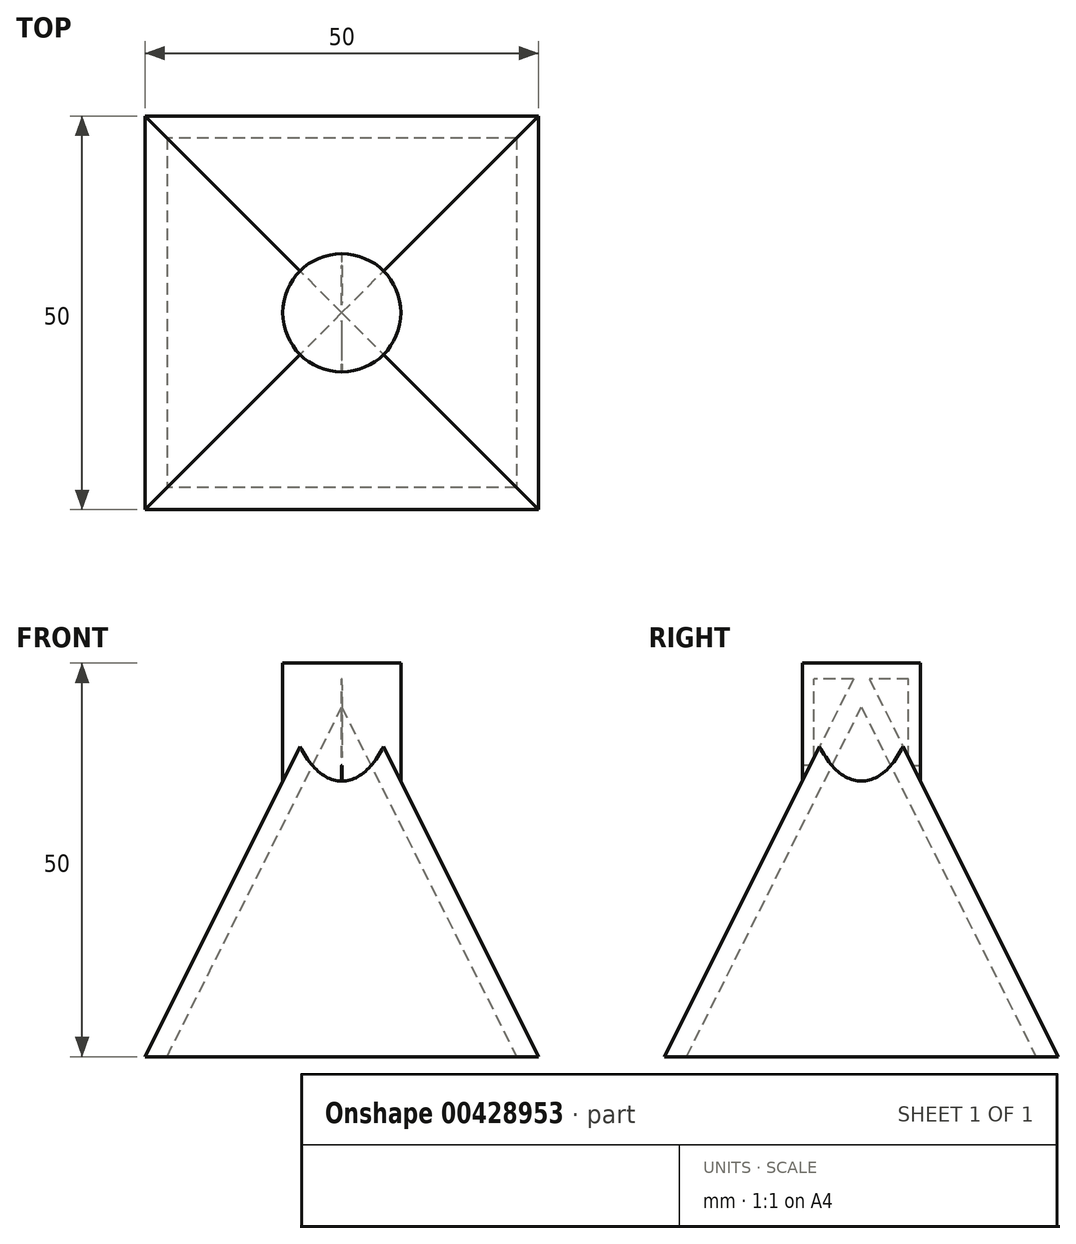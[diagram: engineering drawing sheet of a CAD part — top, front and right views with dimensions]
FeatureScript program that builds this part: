
annotation { "Feature Type Name" : "Feature", "Feature Type Description" : "" }
export const myFeature = defineFeature(function(context is Context, id is Id, definition is map)
    precondition{}
    {
        {
            var Q0;
            Q0=qCreatedBy(makeId("Top.planeOp"),FACE);
            var sketch = newSketch(context, id + "F0", { "sketchPlane" : qUnion([Q0])});
            skLineSegment(sketch, "E0.bottom", {"start": v(25, 25) * mm, "end": v(-25, 25) * mm});
            skLineSegment(sketch, "E0.top", {"start": v(25, -25) * mm, "end": v(-25, -25) * mm});
            skLineSegment(sketch, "E0.left", {"start": v(25, 25) * mm, "end": v(25, -25) * mm});
            skLineSegment(sketch, "E0.right", {"start": v(-25, 25) * mm, "end": v(-25, -25) * mm});
            skPoint(sketch, "E0.middle", {"position": v(0, 0) * mm});
            skSolve(sketch);
        }
        {
            var Q0;
            Q0=makeQuery(id+"F0.imprint","IMPRINT",FACE,{"disambiguationData":[TD([[makeQuery(id+"F0.imprint","IMPRINT",EDGE,{"derivedFrom":sQuery(id+"F0.wireOp",EDGE,"E0.bottom")}),1.0]])]});
            extrude(context, id + "F1", {"entities" : qUnion([Q0]), "depth" : 50 * mm});
        }
        {
            var Q0;
            Q0=makeQuery(id+"F1.opExtrude","SWEPT_FACE",FACE,{"disambiguationData":[OSD([sQuery(id+"F0.wireOp",EDGE,"E0.top")])]});
            var sketch = newSketch(context, id + "F2", { "sketchPlane" : qUnion([Q0])});
            skLineSegment(sketch, "E1", {"start": v(-25, 0) * mm, "end": v(0, 50) * mm});
            skLineSegment(sketch, "E2", {"start": v(0, 50) * mm, "end": v(-25, 50) * mm});
            skLineSegment(sketch, "E3", {"start": v(-25, 50) * mm, "end": v(-25, 0) * mm});
            skLineSegment(sketch, "E4", {"start": v(0, 50) * mm, "end": v(25, 0) * mm});
            skLineSegment(sketch, "E5", {"start": v(25, 0) * mm, "end": v(25, 50) * mm});
            skLineSegment(sketch, "E6", {"start": v(25, 50) * mm, "end": v(0, 50) * mm});
            skSolve(sketch);
        }
        {
            var Q0;
            Q0=makeQuery(id+"F1.opExtrude","SWEPT_FACE",FACE,{"disambiguationData":[OSD([sQuery(id+"F0.wireOp",EDGE,"E0.left")])]});
            var sketch = newSketch(context, id + "F3", { "sketchPlane" : qUnion([Q0])});
            skLineSegment(sketch, "E7", {"start": v(-25, 0) * mm, "end": v(0, 50) * mm});
            skLineSegment(sketch, "E8", {"start": v(0, 50) * mm, "end": v(-25, 50) * mm});
            skLineSegment(sketch, "E9", {"start": v(-25, 50) * mm, "end": v(-25, 1.34) * mm});
            skLineSegment(sketch, "E10", {"start": v(0, 50) * mm, "end": v(25, 50) * mm});
            skLineSegment(sketch, "E11", {"start": v(25, 50) * mm, "end": v(25, 0) * mm});
            skLineSegment(sketch, "E12", {"start": v(25, 0) * mm, "end": v(0, 50) * mm});
            skSolve(sketch);
        }
        {
            var Q0;
            {var subQ0=sQuery(id+"F3.wireOp",EDGE,"E7");Q0=makeQuery(id+"F3.imprint","IMPRINT",FACE,{"disambiguationData":[TD([[makeQuery(id+"F3.imprint","IMPRINT",EDGE,{"derivedFrom":subQ0}),1.0]])]});}
            var Q1;
            Q1=makeQuery(id+"F3.imprint","IMPRINT",FACE,{"disambiguationData":[TD([[makeQuery(id+"F3.imprint","IMPRINT",EDGE,{"derivedFrom":sQuery(id+"F3.wireOp",EDGE,"E10")}),1.0]])]});
            var Q2;
            Q2=makeQuery(id+"F1.opExtrude","SWEPT_FACE",FACE,{"disambiguationData":[OSD([sQuery(id+"F0.wireOp",EDGE,"E0.right")])]});
            extrude(context, id + "F4", {"entities" : qUnion([Q0, Q1]), "operationType" : NewBodyOperationType.REMOVE, "endBound" : BoundingType.UP_TO_SURFACE, "oppositeDirection" : true, "endBoundEntityFace" : qUnion([Q2]), "depth" : 25 * mm});
        }
        {
            var Q0;
            Q0=makeQuery(id+"F2.imprint","IMPRINT",FACE,{"disambiguationData":[TD([[makeQuery(id+"F2.imprint","IMPRINT",EDGE,{"derivedFrom":sQuery(id+"F2.wireOp",EDGE,"E1")}),1.0]])]});
            var Q1;
            Q1=makeQuery(id+"F2.imprint","IMPRINT",FACE,{"disambiguationData":[TD([[makeQuery(id+"F2.imprint","IMPRINT",EDGE,{"derivedFrom":sQuery(id+"F2.wireOp",EDGE,"E4")}),1.0]])]});
            var Q2;
            Q2=makeQuery(id+"F4.boolean.opBoolean","COPY",FACE,{"derivedFrom":makeQuery(id+"F4.opExtrude","SWEPT_FACE",FACE,{"disambiguationData":[OSD([sQuery(id+"F3.wireOp",EDGE,"E12")])]})});
            extrude(context, id + "F5", {"entities" : qUnion([Q0, Q1]), "operationType" : NewBodyOperationType.REMOVE, "endBound" : BoundingType.UP_TO_SURFACE, "oppositeDirection" : true, "endBoundEntityFace" : qUnion([Q2]), "depth" : 25 * mm});
        }
        {
            var Q0;
            Q0=makeQuery(id+"F1.opExtrude","CAP_FACE",FACE,{"disambiguationData":[OSD([sQuery(id+"F0.wireOp",EDGE,"E0.bottom"),sQuery(id+"F0.wireOp",EDGE,"E0.top"),sQuery(id+"F0.wireOp",EDGE,"E0.left"),sQuery(id+"F0.wireOp",EDGE,"E0.right")])],"isStart":true});
            shell(context, id + "F6", {"entities" : qUnion([Q0]), "thickness" : 2.5 * mm});
        }
        {
            var Q0;
            Q0=qCreatedBy(makeId("Front.planeOp"),FACE);
            var sketch = newSketch(context, id + "F7", { "sketchPlane" : qUnion([Q0])});
            skLineSegment(sketch, "E13.bottom", {"start": v(-7.5, 35) * mm, "end": v(7.5, 35) * mm});
            skLineSegment(sketch, "E13.top", {"start": v(-7.5, 50) * mm, "end": v(7.5, 50) * mm});
            skLineSegment(sketch, "E13.left", {"start": v(-7.5, 35) * mm, "end": v(-7.5, 50) * mm});
            skLineSegment(sketch, "E13.right", {"start": v(7.5, 35) * mm, "end": v(7.5, 50) * mm});
            skLineSegment(sketch, "E14", {"start": v(-7.5, 35) * mm, "end": v(0, 50) * mm});
            skLineSegment(sketch, "E15", {"start": v(0, 50) * mm, "end": v(7.5, 35) * mm});
            skLineSegment(sketch, "E16", {"start": v(0, 50) * mm, "end": v(0, 35) * mm});
            skSolve(sketch);
        }
        {
            var Q0;
            {var subQ0=sQuery(id+"F7.wireOp",EDGE,"E13.left");Q0=makeQuery(id+"F7.imprint","IMPRINT",FACE,{"disambiguationData":[TD([[makeQuery(id+"F7.imprint","IMPRINT",EDGE,{"derivedFrom":subQ0}),-1.0]])]});}
            var Q1;
            {var subQ0=sQuery(id+"F7.wireOp",EDGE,"E13.right");Q1=makeQuery(id+"F7.imprint","IMPRINT",FACE,{"disambiguationData":[TD([[makeQuery(id+"F7.imprint","IMPRINT",EDGE,{"derivedFrom":subQ0}),1.0]])]});}
            var Q2;
            Q2=sQuery(id+"F7.wireOp",EDGE,"E16");
            revolve(context, id + "F8", {"operationType" : NewBodyOperationType.ADD, "entities" : qUnion([Q0, Q1]), "axis" : qUnion([Q2]), "revolveType" : RevolveType.SYMMETRIC, "angle" : 179.9 * degree});
        }
        {
            var Q0;
            {var subQ0=sQuery(id+"F7.wireOp",EDGE,"E13.top");Q0=makeQuery(id+"F8.opRevolve","SWEPT_FACE",FACE,{"disambiguationData":[OSD([subQ0]),TDD([makeQuery(id+"F7.imprint","IMPRINT",EDGE,{"disambiguationData":[TD([[makeQuery(id+"F7.imprint","INTERSECT",VERTEX,{"derivedFrom":[subQ0,sQuery(id+"F7.wireOp",EDGE,"E13.left")]}),-1.0]])],"derivedFrom":subQ0})])]});}
            var sketch = newSketch(context, id + "F9", { "sketchPlane" : qUnion([Q0])});
            skCircle(sketch, "E17", {"center": v(0, 0) * mm, "radius": 7.5 * mm});
            skSolve(sketch);
        }
        {
            var Q0;
            {var subQ1=sQuery(id+"F7.wireOp",EDGE,"E13.top");var subQ2=makeQuery(id+"F7.imprint","IMPRINT",EDGE,{"disambiguationData":[TD([[makeQuery(id+"F7.imprint","INTERSECT",VERTEX,{"derivedFrom":[subQ1,sQuery(id+"F7.wireOp",EDGE,"E13.left")]}),-1.0]])],"derivedFrom":subQ1});var subQ3=makeQuery(id+"F8.opRevolve","CAP_EDGE",EDGE,{"disambiguationData":[OSD([subQ1]),TDD([subQ2]),OD(0.0)],"isStart":false});Q0=makeQuery(id+"F9.imprint","IMPRINT",FACE,{"disambiguationData":[TD([[makeQuery(id+"F9.imprint","IMPRINT",EDGE,{"derivedFrom":subQ3}),1.0]])]});}
            var Q1;
            {var subQ1=sQuery(id+"F7.wireOp",EDGE,"E13.top");var subQ2=makeQuery(id+"F7.imprint","IMPRINT",EDGE,{"disambiguationData":[TD([[makeQuery(id+"F7.imprint","INTERSECT",VERTEX,{"derivedFrom":[subQ1,sQuery(id+"F7.wireOp",EDGE,"E13.left")]}),-1.0]])],"derivedFrom":subQ1});var subQ3=makeQuery(id+"F8.opRevolve","CAP_EDGE",EDGE,{"disambiguationData":[OSD([subQ1]),TDD([subQ2]),OD(0.0)],"isStart":false});Q1=makeQuery(id+"F9.imprint","IMPRINT",FACE,{"disambiguationData":[TD([[makeQuery(id+"F9.imprint","IMPRINT",EDGE,{"derivedFrom":subQ3}),-1.0]])]});}
            extrude(context, id + "F10", {"entities" : qUnion([Q0, Q1]), "operationType" : NewBodyOperationType.ADD, "oppositeDirection" : true, "depth" : 2 * mm});
        }
        {
            var Q0;
            {var subQ0=sQuery(id+"F7.wireOp",EDGE,"E13.top");Q0=makeQuery(id+"F10.boolean.opBoolean","MERGE",FACE,{"derivedFrom":[makeQuery(id+"F8.opRevolve","SWEPT_FACE",FACE,{"disambiguationData":[OSD([subQ0]),TDD([makeQuery(id+"F7.imprint","IMPRINT",EDGE,{"disambiguationData":[TD([[makeQuery(id+"F7.imprint","INTERSECT",VERTEX,{"derivedFrom":[subQ0,sQuery(id+"F7.wireOp",EDGE,"E13.left")]}),-1.0]])],"derivedFrom":subQ0})])]}),makeQuery(id+"F8.opRevolve","SWEPT_FACE",FACE,{"disambiguationData":[OSD([subQ0]),TDD([makeQuery(id+"F7.imprint","IMPRINT",EDGE,{"disambiguationData":[TD([[makeQuery(id+"F7.imprint","INTERSECT",VERTEX,{"derivedFrom":[subQ0,sQuery(id+"F7.wireOp",EDGE,"E13.right")]}),1.0]])],"derivedFrom":subQ0})])]}),makeQuery(id+"F10.opExtrude","CAP_FACE",FACE,{"disambiguationData":[OSD([sQuery(id+"F9.wireOp",EDGE,"E17")])],"isStart":true})]});}
            var sketch = newSketch(context, id + "F11", { "sketchPlane" : qUnion([Q0])});
            skCircle(sketch, "E18", {"center": v(0, 0) * mm, "radius": 6 * mm});
            skCircle(sketch, "E19", {"center": v(0, 0) * mm, "radius": 7.5 * mm});
            skSolve(sketch);
        }
        {
            var Q0;
            Q0=makeQuery(id+"F11.imprint","IMPRINT",FACE,{"disambiguationData":[TD([[makeQuery(id+"F11.imprint","IMPRINT",EDGE,{"derivedFrom":sQuery(id+"F11.wireOp",EDGE,"E18")}),-1.0]])]});
            extrude(context, id + "F12", {"entities" : qUnion([Q0]), "operationType" : NewBodyOperationType.ADD, "oppositeDirection" : true, "depth" : 13 * mm});
        }
    });
